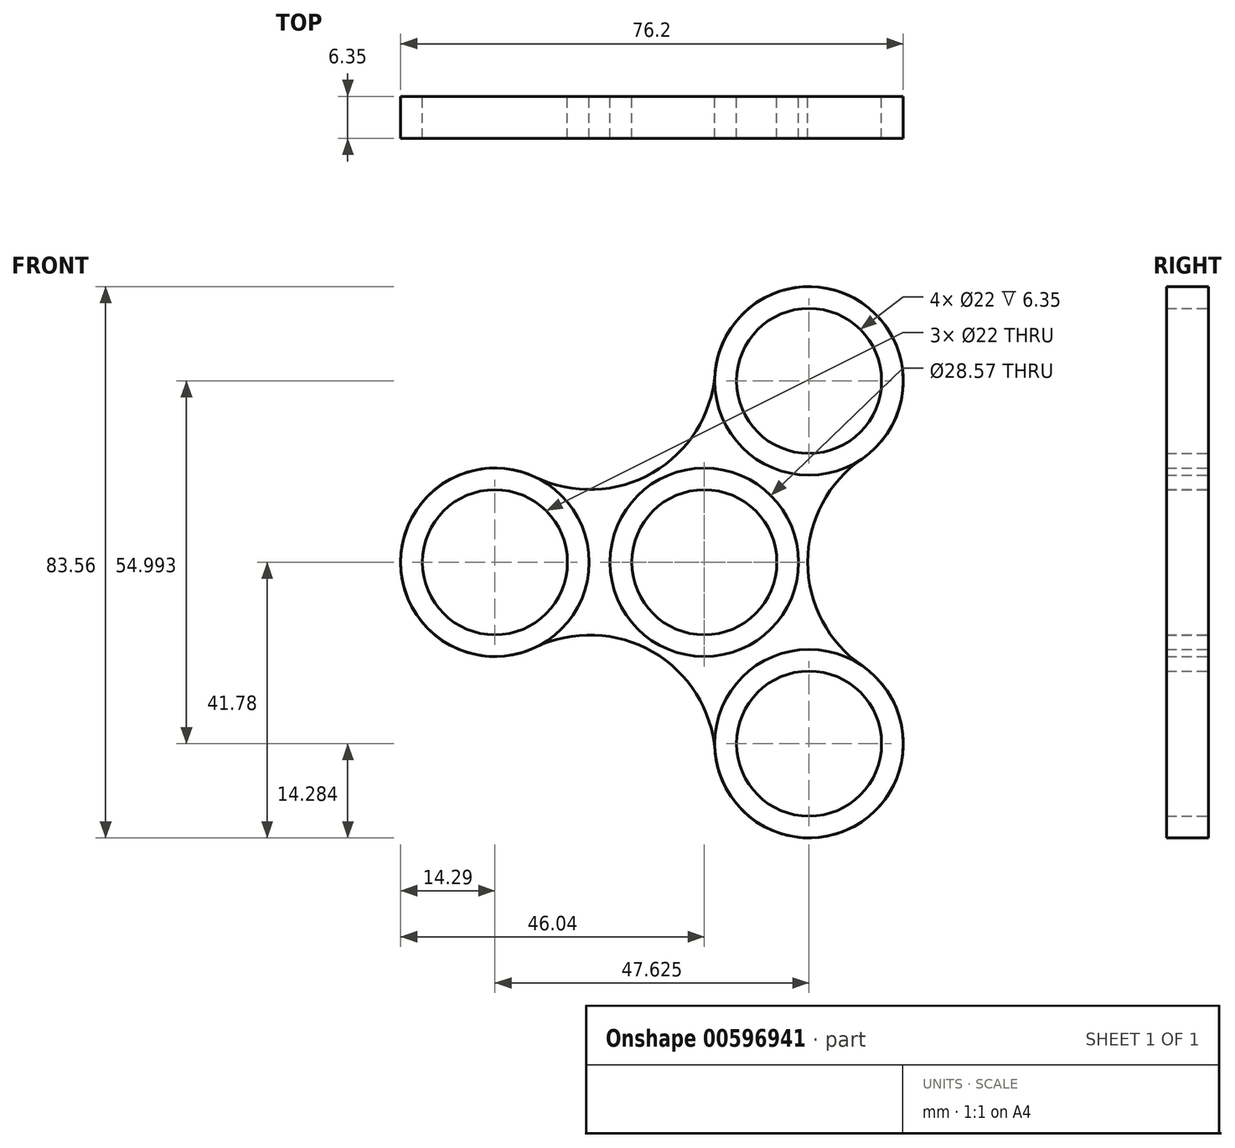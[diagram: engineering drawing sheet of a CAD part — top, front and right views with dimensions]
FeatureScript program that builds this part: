
annotation { "Feature Type Name" : "Feature", "Feature Type Description" : "" }
export const myFeature = defineFeature(function(context is Context, id is Id, definition is map)
    precondition{}
    {
        {
            var Q0;
            Q0=qCreatedBy(makeId("Front.planeOp"),FACE);
            var sketch = newSketch(context, id + "F0", { "sketchPlane" : qUnion([Q0])});
            skCircle(sketch, "E0", {"center": v(0, 0) * mm, "radius": 14.29 * mm});
            skCircle(sketch, "E1", {"center": v(0, 0) * mm, "radius": 11 * mm});
            skCircle(sketch, "E2", {"center": v(-31.75, 0) * mm, "radius": 14.29 * mm});
            skCircle(sketch, "E3", {"center": v(-31.75, 0) * mm, "radius": 11 * mm});
            skCircle(sketch, "E4.1.0", {"center": v(15.87, -27.5) * mm, "radius": 11 * mm});
            skCircle(sketch, "E4.1.1", {"center": v(15.87, -27.5) * mm, "radius": 14.29 * mm});
            skCircle(sketch, "E4.2.0", {"center": v(15.88, 27.5) * mm, "radius": 11 * mm});
            skCircle(sketch, "E4.2.1", {"center": v(15.88, 27.5) * mm, "radius": 14.29 * mm});
            skLineSegment(sketch, "E5", {"start": v(15.88, 27.5) * mm, "end": v(0, 0) * mm});
            skCircle(sketch, "E6", {"center": v(0, 0) * mm, "radius": 31.75 * mm});
            skCircle(sketch, "E7", {"center": v(0, 0) * mm, "radius": 26.99 * mm});
            skSolve(sketch);
        }
        {
            var Q0;
            Q0=qCreatedBy(makeId("Front.planeOp"),FACE);
            var sketch = newSketch(context, id + "F1", { "sketchPlane" : qUnion([Q0])});
            skArc(sketch, "E8", {"start": v(-25.58, 12.89) * mm, "mid": v(-7.84, 13.58) * mm, "end": v(1.63, 28.6) * mm});
            skArc(sketch, "E9", {"start": v(23.95, 15.71) * mm, "mid": v(15.68, 0) * mm, "end": v(23.95, -15.71) * mm});
            skArc(sketch, "E10", {"start": v(1.63, -28.6) * mm, "mid": v(-7.84, -13.58) * mm, "end": v(-25.58, -12.89) * mm});
            skCircle(sketch, "E11.0", {"center": v(15.88, 27.5) * mm, "radius": 14.29 * mm});
            skCircle(sketch, "E12.0", {"center": v(15.87, -27.5) * mm, "radius": 14.29 * mm});
            skCircle(sketch, "E13.0", {"center": v(-31.75, 0) * mm, "radius": 14.29 * mm});
            skCircle(sketch, "E14.0", {"center": v(-31.75, 0) * mm, "radius": 11 * mm});
            skCircle(sketch, "E15.0", {"center": v(0, 0) * mm, "radius": 11 * mm});
            skCircle(sketch, "E16.0", {"center": v(0, 0) * mm, "radius": 14.29 * mm});
            skCircle(sketch, "E17.0", {"center": v(15.88, 27.5) * mm, "radius": 11 * mm});
            skCircle(sketch, "E18.0", {"center": v(15.87, -27.5) * mm, "radius": 11 * mm});
            skSolve(sketch);
        }
        {
            var Q0;
            Q0=makeQuery(id+"F1.imprint","IMPRINT",FACE,{"disambiguationData":[TD([[makeQuery(id+"F1.imprint","IMPRINT",EDGE,{"derivedFrom":sQuery(id+"F1.wireOp",EDGE,"E17.0")}),-1.0]])]});
            var Q1;
            Q1=makeQuery(id+"F1.imprint","IMPRINT",FACE,{"disambiguationData":[TD([[makeQuery(id+"F1.imprint","IMPRINT",EDGE,{"derivedFrom":sQuery(id+"F1.wireOp",EDGE,"E18.0")}),-1.0]])]});
            var Q2;
            Q2=makeQuery(id+"F1.imprint","IMPRINT",FACE,{"disambiguationData":[TD([[makeQuery(id+"F1.imprint","IMPRINT",EDGE,{"derivedFrom":sQuery(id+"F1.wireOp",EDGE,"E14.0")}),-1.0]])]});
            var Q3;
            Q3=makeQuery(id+"F0.imprint","IMPRINT",FACE,{"disambiguationData":[TD([[makeQuery(id+"F0.imprint","IMPRINT",EDGE,{"derivedFrom":sQuery(id+"F0.wireOp",EDGE,"E2")}),1.0]])]});
            var Q4;
            Q4=makeQuery(id+"F0.imprint","IMPRINT",FACE,{"disambiguationData":[TD([[makeQuery(id+"F0.imprint","IMPRINT",EDGE,{"derivedFrom":sQuery(id+"F0.wireOp",EDGE,"E1")}),-1.0]])]});
            var Q5;
            Q5=makeQuery(id+"F0.imprint","IMPRINT",FACE,{"disambiguationData":[TD([[makeQuery(id+"F0.imprint","IMPRINT",EDGE,{"derivedFrom":sQuery(id+"F0.wireOp",EDGE,"E4.2.0")}),-1.0]])]});
            var Q6;
            Q6=makeQuery(id+"F0.imprint","IMPRINT",FACE,{"disambiguationData":[TD([[makeQuery(id+"F0.imprint","IMPRINT",EDGE,{"derivedFrom":sQuery(id+"F0.wireOp",EDGE,"E4.1.0")}),-1.0]])]});
            var Q7;
            {var subQ1=sQuery(id+"F1.wireOp",EDGE,"E8");Q7=makeQuery(id+"F1.imprint","IMPRINT",FACE,{"disambiguationData":[TD([[makeQuery(id+"F1.imprint","IMPRINT",EDGE,{"derivedFrom":subQ1}),-1.0]])]});}
            extrude(context, id + "F2", {"entities" : qUnion([Q0, Q1, Q2, Q3, Q4, Q5, Q6, Q7]), "depth" : 6.35 * mm, "offsetDistance" : 25.4 * mm});
        }
    });
